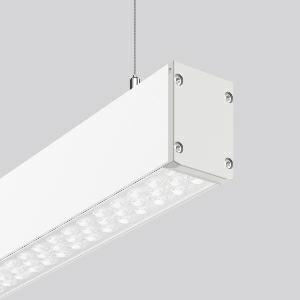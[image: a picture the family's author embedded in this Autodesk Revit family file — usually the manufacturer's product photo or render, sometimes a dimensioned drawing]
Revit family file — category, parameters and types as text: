
# Revit family: linedo_single_ip54_312566_002_76_28db
name_source: partatom
category: Lighting Fixtures
units: mm (PartAtom-declared; Revit-internal decimal feet)

## family parameters
Cut with Voids When Loaded = No
Host = Face
Light Source = No
Part Type = Normal
Room Calculation Point = No
Round Connector Dimension = Use Diameter
Shared = No

## types (1)
- LINEDO single IP54 (1 x LED Modul 830, 6100 lm, 3000)
    Apparent Load = 40 VA
    CIE Flux Codes = 86 96 99 100 100
    Color Rendering = 80
    Color Temperature = 3000
    Default Elevation = 1800 mm
    Description = Series: LINEDO single IP54
Stylish pendant luminaire. Housing: extruded aluminium profile, powder-coated. Plastic end caps, grey. High-efficiency LED units with optimum light control thanks to clear plastic (PC) lens optics. 2-point steel cable suspension freely positionable and infinitely height-adjustable. With power cord (2.5 m). Please order canopy separately if required. Perfect for office areas (RUG < 19) and environments with computer screens in accordance with EN 12464-1. Luminaire with limited surface temperature in accordance with EN 60598-2-24 for use in environments in which a deposit of conductive dust on the luminaire can be expected. 
Colour: traffic white, matt (RAL 9016)
Length: 2274 mm
Width: 58 mm
Height: 76 mm
Suspension length: 100-1500 mm
Lamp: LED
Socket: without socket
Colour temperature: 3000K
Colour rendering index (CRI): 80
System power: 40 W
Rated luminous flux: 6100 lm
Beam angle Down: 59°
Luminous efficiency: 153 lm/W
Control gear: Converter, dimmable, DALI
Protection class: I
Type of protection: IP 54
    Height = 76 mm
    Lamp = 1 x LED Modul 830
    Lamp Light Flux = 6100 lm
    Lamp count = 1
    Length = 2274 mm
    Lifetime = 50000 h
    Luminous efficacy = 153 lm/W
    Manufacturer = RZB
    ModVariant = No
    Model = 312566.002.76
    Mounting Place = Ceiling
    Mounting Type = Surface mounted, Pendant
    Number of Poles = 1
    OnlyDefault = Yes
    Power Factor = 1
    Product Name = LINEDO single IP54
    Product group = Pendant luminaires
    ProductGroupID = 902
    Protection Class = Protection class I
    Protection Degree = IP 54
    RLX_Detail_Level = 1
    RLX_Emergency_Light_Flux = 0 lm
    RLX_Emergency_Type = 0
    RLX_Emergency_Type_DB = No
    RlxData = <blob elided: 27017 chars, md5=d4fb181d>
    Socket = socket
    Standby Power = 0 W
    System Light Flux = 6100 lm
    System Power = 40 W
    Type Comments = ALEA SPOT
    Type Image = 312565.002.jpg
    URL = http://relux.com
    VarID = ---
    Voltage = 230 V
    Voltage Range = 220-240 V
    Weight = 0.00 kg
    Width = 58 mm

## geometry (parser evidence)
native form markers: Blend x4, Sweep x12
no freeform markers — native parametric forms only
